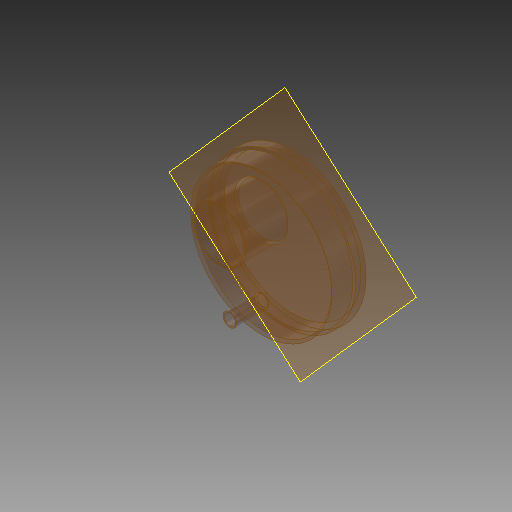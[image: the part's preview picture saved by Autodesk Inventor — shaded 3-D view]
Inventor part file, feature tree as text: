
AUTODESK INVENTOR PART (.ipt)
format: ipt  version: 2019 (Build 230136000, 136)  size: 152,576 bytes
history: native  units: mm
features: other x7, extrude x6, sketch x6
ambient origin geometry x8: Origin, YZ Plane, XZ Plane, XY Plane, X Axis, Y Axis, Z Axis, Center Point
bodies: Body1 (feature_tree)
feature tree (19):
  other  "Sólido1"
  other  "Plano de trabalho1"
  extrude  "Extrusão1"  Depth=5.0mm TaperAngle=0.0deg
  extrude  "Extrusão2"  Depth=10.0mm TaperAngle=0.0deg
  extrude  "Extrusão3"  Depth=1.0mm
  extrude  "Extrusão4"  Depth=20.0mm TaperAngle=0.0deg
  extrude  "Extrusão5"  Depth=0.5mm
  extrude  "Extrusão6"  Depth=15.0mm TaperAngle=0.0deg
  sketch  "Esboço1"  dims[d0=70.0mm d1=5.0mm d2=0.0mm]
  other  "Referência1"
  sketch  "Esboço2"  dims[d3=1.0mm d4=10.0mm d5=0.0mm]
  other  "Referência2"
  sketch  "Esboço3"  dims[d6=1.0mm d7=0.0mm d8=25.5mm]
  sketch  "Esboço4"  dims[d9=1.0mm d10=20.0mm d11=0.0mm]
  sketch  "Esboço5"  dims[d12=6.5mm d14=0.5mm]
  other  "Contorno projetado1"
  sketch  "Esboço6"  dims[d15=20.0mm d16=15.0mm d17=0.0mm d18=15.0mm d19=0.0mm]
  other  "Conjunto Ambu.iam"
  other  "Corpo do Ambu:1"
